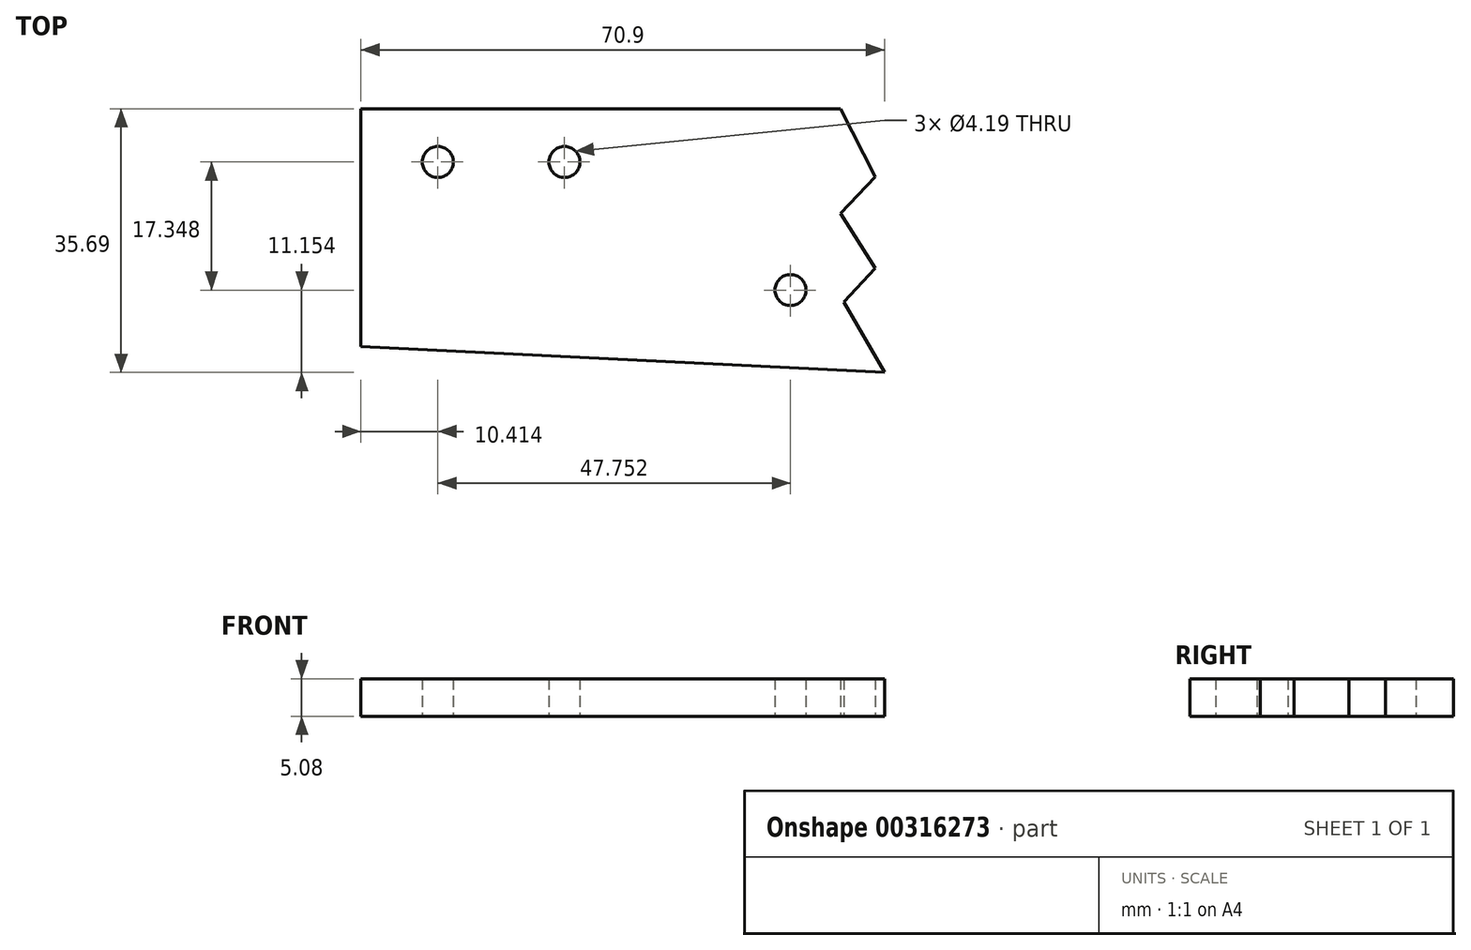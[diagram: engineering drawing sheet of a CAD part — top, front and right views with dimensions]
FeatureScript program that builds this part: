
annotation { "Feature Type Name" : "Feature", "Feature Type Description" : "" }
export const myFeature = defineFeature(function(context is Context, id is Id, definition is map)
    precondition{}
    {
        {
            var Q0;
            Q0=qCreatedBy(makeId("Top.planeOp"),FACE);
            var sketch = newSketch(context, id + "F0", { "sketchPlane" : qUnion([Q0])});
            skLineSegment(sketch, "E0.bottom", {"start": v(0, 0) * mm, "end": v(64.92, 0) * mm});
            skLineSegment(sketch, "E0.top", {"start": v(0, -32.2) * mm, "end": v(70.9, -35.7) * mm});
            skLineSegment(sketch, "E0.left", {"start": v(0, 0) * mm, "end": v(0, -32.2) * mm});
            skLineSegment(sketch, "E1", {"start": v(0, -7.19) * mm, "end": v(29.65, -7.19) * mm, "construction": true});
            skLineSegment(sketch, "E2", {"start": v(0, -24.54) * mm, "end": v(58.17, -24.54) * mm, "construction": true});
            skLineSegment(sketch, "E3", {"start": v(10.41, 0) * mm, "end": v(10.41, -9.28) * mm, "construction": true});
            skLineSegment(sketch, "E4", {"start": v(27.56, 0) * mm, "end": v(27.56, -9.28) * mm, "construction": true});
            skLineSegment(sketch, "E5", {"start": v(58.17, 0) * mm, "end": v(58.17, -24.54) * mm, "construction": true});
            skCircle(sketch, "E6", {"center": v(10.41, -7.19) * mm, "radius": 2.1 * mm});
            skCircle(sketch, "E7", {"center": v(27.56, -7.19) * mm, "radius": 2.1 * mm});
            skCircle(sketch, "E8", {"center": v(58.17, -24.54) * mm, "radius": 2.1 * mm});
            skLineSegment(sketch, "E9", {"start": v(64.92, 0) * mm, "end": v(69.67, -9.21) * mm});
            skLineSegment(sketch, "E10", {"start": v(69.67, -9.21) * mm, "end": v(64.92, -14.16) * mm});
            skLineSegment(sketch, "E11", {"start": v(64.92, -14.16) * mm, "end": v(69.67, -21.59) * mm});
            skLineSegment(sketch, "E12", {"start": v(69.67, -21.59) * mm, "end": v(64.92, -26.66) * mm});
            skLineSegment(sketch, "E13", {"start": v(65.4, -26.14) * mm, "end": v(70.9, -35.7) * mm});
            skSolve(sketch);
        }
        {
            var Q0;
            Q0=makeQuery(id+"F0.imprint","IMPRINT",FACE,{"disambiguationData":[TD([[makeQuery(id+"F0.imprint","IMPRINT",EDGE,{"derivedFrom":sQuery(id+"F0.wireOp",EDGE,"E0.bottom")}),-1.0]])]});
            extrude(context, id + "F1", {"entities" : qUnion([Q0]), "depth" : 5.08 * mm});
        }
    });
